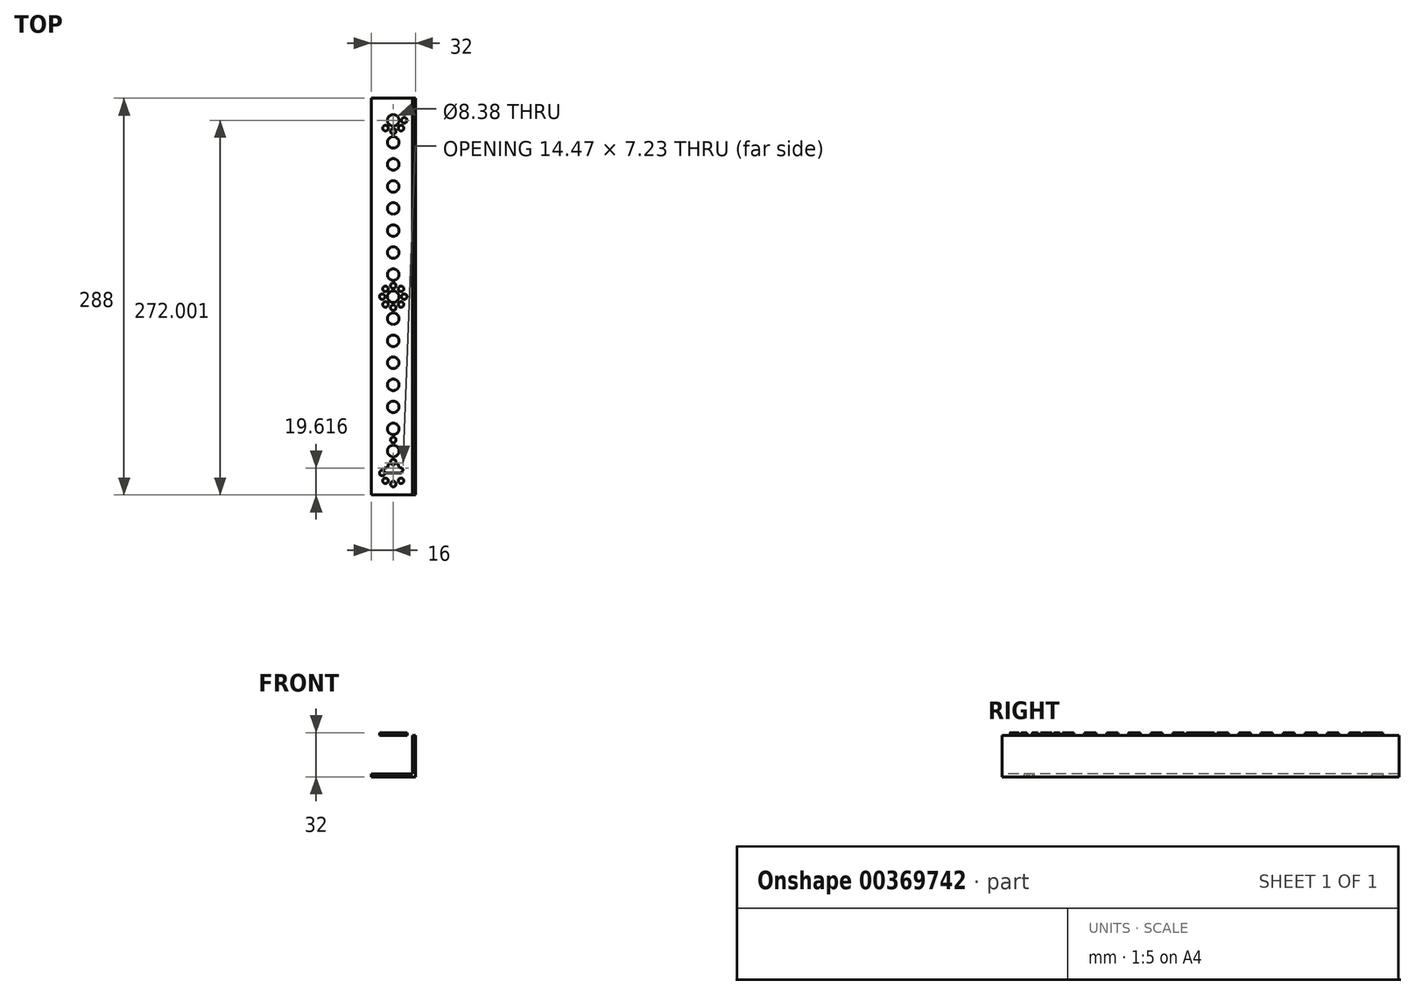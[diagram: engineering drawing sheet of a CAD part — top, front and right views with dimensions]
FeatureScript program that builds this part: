
annotation { "Feature Type Name" : "Feature", "Feature Type Description" : "" }
export const myFeature = defineFeature(function(context is Context, id is Id, definition is map)
    precondition{}
    {
        {
            var Q0;
            Q0=qCreatedBy(makeId("Front.planeOp"),FACE);
            var sketch = newSketch(context, id + "F0", { "sketchPlane" : qUnion([Q0])});
            skLineSegment(sketch, "E0.bottom", {"start": v(0, 0) * mm, "end": v(32, 0) * mm});
            skLineSegment(sketch, "E0.top", {"start": v(0, 32) * mm, "end": v(32, 32) * mm});
            skLineSegment(sketch, "E0.left", {"start": v(0, 0) * mm, "end": v(0, 32) * mm});
            skLineSegment(sketch, "E0.right", {"start": v(32, 0) * mm, "end": v(32, 32) * mm});
            skSolve(sketch);
        }
        {
            var Q0;
            Q0=makeQuery(id+"F0.imprint","IMPRINT",FACE,{"disambiguationData":[TD([[makeQuery(id+"F0.imprint","IMPRINT",EDGE,{"derivedFrom":sQuery(id+"F0.wireOp",EDGE,"E0.bottom")}),1.0]])]});
            extrude(context, id + "F1", {"entities" : qUnion([Q0]), "oppositeDirection" : true, "depth" : 288 * mm});
        }
        {
            var Q0;
            Q0=makeQuery(id+"F1.opExtrude","SWEPT_FACE",FACE,{"disambiguationData":[OSD([sQuery(id+"F0.wireOp",EDGE,"E0.left")])]});
            var Q1;
            Q1=makeQuery(id+"F1.opExtrude","CAP_FACE",FACE,{"disambiguationData":[OSD([sQuery(id+"F0.wireOp",EDGE,"E0.bottom"),sQuery(id+"F0.wireOp",EDGE,"E0.top"),sQuery(id+"F0.wireOp",EDGE,"E0.left"),sQuery(id+"F0.wireOp",EDGE,"E0.right")])],"isStart":true});
            var Q2;
            Q2=makeQuery(id+"F1.opExtrude","CAP_FACE",FACE,{"disambiguationData":[OSD([sQuery(id+"F0.wireOp",EDGE,"E0.bottom"),sQuery(id+"F0.wireOp",EDGE,"E0.top"),sQuery(id+"F0.wireOp",EDGE,"E0.left"),sQuery(id+"F0.wireOp",EDGE,"E0.right")])],"isStart":false});
            shell(context, id + "F2", {"entities" : qUnion([Q0, Q1, Q2]), "thickness" : 2 * mm});
        }
        {
            var Q0;
            Q0=makeQuery(id+"F1.opExtrude","SWEPT_FACE",FACE,{"disambiguationData":[OSD([sQuery(id+"F0.wireOp",EDGE,"E0.bottom")])]});
            var sketch = newSketch(context, id + "F3", { "sketchPlane" : qUnion([Q0])});
            skLineSegment(sketch, "E1.0", {"start": v(0, 0) * mm, "end": v(32, 0) * mm});
            skLineSegment(sketch, "E2.0", {"start": v(0, -288) * mm, "end": v(0, 0) * mm});
            skLineSegment(sketch, "E3.0", {"start": v(32, -288) * mm, "end": v(32, 0) * mm});
            skLineSegment(sketch, "E4.0", {"start": v(0, -288) * mm, "end": v(32, -288) * mm});
            skLineSegment(sketch, "E5", {"start": v(16, 0) * mm, "end": v(16, -288) * mm});
            skLineSegment(sketch, "E6", {"start": v(0, -144) * mm, "end": v(32, -144) * mm});
            skCircle(sketch, "E7", {"center": v(16, -16) * mm, "radius": 4.2 * mm});
            skCircle(sketch, "E8.cCircle", {"center": v(16, -16) * mm, "radius": 8 * mm, "construction": true});
            skLineSegment(sketch, "E8.0", {"start": v(24, -16) * mm, "end": v(21.66, -21.66) * mm});
            skLineSegment(sketch, "E8.1", {"start": v(21.66, -21.66) * mm, "end": v(16, -24) * mm});
            skLineSegment(sketch, "E8.2", {"start": v(16, -24) * mm, "end": v(10.34, -21.66) * mm});
            skLineSegment(sketch, "E8.3", {"start": v(10.34, -21.66) * mm, "end": v(8, -16) * mm});
            skLineSegment(sketch, "E8.4", {"start": v(8, -16) * mm, "end": v(10.34, -10.34) * mm});
            skLineSegment(sketch, "E8.5", {"start": v(10.34, -10.34) * mm, "end": v(16, -8) * mm});
            skLineSegment(sketch, "E8.6", {"start": v(16, -8) * mm, "end": v(21.66, -10.34) * mm});
            skLineSegment(sketch, "E8.7", {"start": v(21.66, -10.34) * mm, "end": v(24, -16) * mm});
            skLineSegment(sketch, "E9", {"start": v(16, -16) * mm, "end": v(32, -16) * mm});
            skLineSegment(sketch, "E10", {"start": v(32, -16) * mm, "end": v(0, -16) * mm});
            skCircle(sketch, "E11", {"center": v(16, -8) * mm, "radius": 2 * mm});
            skCircle(sketch, "E12", {"center": v(21.66, -10.34) * mm, "radius": 2 * mm});
            skCircle(sketch, "E13", {"center": v(24, -16) * mm, "radius": 2 * mm});
            skCircle(sketch, "E14", {"center": v(10.34, -10.34) * mm, "radius": 2 * mm});
            skCircle(sketch, "E15", {"center": v(8, -16) * mm, "radius": 2 * mm});
            skCircle(sketch, "E16.MirrorC", {"center": v(10.34, -21.66) * mm, "radius": 2 * mm});
            skCircle(sketch, "E17.MirrorC", {"center": v(16, -24) * mm, "radius": 2 * mm});
            skCircle(sketch, "E18.MirrorC", {"center": v(21.66, -21.66) * mm, "radius": 2 * mm});
            skCircle(sketch, "E19.MirrorC", {"center": v(10.34, -277.66) * mm, "radius": 2 * mm});
            skCircle(sketch, "E20.MirrorC", {"center": v(16, -280) * mm, "radius": 2 * mm});
            skCircle(sketch, "E21.MirrorC", {"center": v(21.66, -277.66) * mm, "radius": 2 * mm});
            skCircle(sketch, "E22.MirrorC", {"center": v(24, -272) * mm, "radius": 2 * mm});
            skCircle(sketch, "E23.MirrorC", {"center": v(21.66, -266.34) * mm, "radius": 2 * mm});
            skCircle(sketch, "E24.MirrorC", {"center": v(16, -264) * mm, "radius": 2 * mm});
            skCircle(sketch, "E25.MirrorC", {"center": v(10.34, -266.34) * mm, "radius": 2 * mm});
            skCircle(sketch, "E26.MirrorC", {"center": v(16, -272) * mm, "radius": 4.2 * mm});
            skCircle(sketch, "E27.MirrorC", {"center": v(8, -272) * mm, "radius": 2 * mm});
            skSolve(sketch);
        }
        {
            var Q0;
            {var subQ0=sQuery(id+"F3.wireOp",EDGE,"E10");var subQ1=sQuery(id+"F3.wireOp",EDGE,"E5");var subQ2=makeQuery(id+"F3.imprint","INTERSECT",VERTEX,{"derivedFrom":[subQ1,subQ0]});Q0=makeQuery(id+"F3.imprint","IMPRINT",FACE,{"disambiguationData":[TD([[makeQuery(id+"F3.imprint","IMPRINT",EDGE,{"disambiguationData":[TD([[subQ2,-1.0]])],"derivedFrom":subQ1}),1.0]])]});}
            var Q1;
            {var subQ0=sQuery(id+"F3.wireOp",EDGE,"E7");var subQ1=sQuery(id+"F3.wireOp",EDGE,"E5");var subQ2=makeQuery(id+"F3.imprint","INTERSECT",VERTEX,{"disambiguationData":[OD(0.0)],"derivedFrom":[subQ1,subQ0]});Q1=makeQuery(id+"F3.imprint","IMPRINT",FACE,{"disambiguationData":[TD([[makeQuery(id+"F3.imprint","IMPRINT",EDGE,{"disambiguationData":[TD([[subQ2,-1.0]])],"derivedFrom":subQ1}),1.0]])]});}
            var Q2;
            {var subQ0=sQuery(id+"F3.wireOp",EDGE,"E7");var subQ1=sQuery(id+"F3.wireOp",EDGE,"E5");var subQ2=makeQuery(id+"F3.imprint","INTERSECT",VERTEX,{"disambiguationData":[OD(0.0)],"derivedFrom":[subQ1,subQ0]});Q2=makeQuery(id+"F3.imprint","IMPRINT",FACE,{"disambiguationData":[TD([[makeQuery(id+"F3.imprint","IMPRINT",EDGE,{"disambiguationData":[TD([[subQ2,-1.0]])],"derivedFrom":subQ1}),-1.0]])]});}
            var Q3;
            {var subQ0=sQuery(id+"F3.wireOp",EDGE,"E10");var subQ1=sQuery(id+"F3.wireOp",EDGE,"E5");var subQ2=makeQuery(id+"F3.imprint","INTERSECT",VERTEX,{"derivedFrom":[subQ1,subQ0]});Q3=makeQuery(id+"F3.imprint","IMPRINT",FACE,{"disambiguationData":[TD([[makeQuery(id+"F3.imprint","IMPRINT",EDGE,{"disambiguationData":[TD([[subQ2,-1.0]])],"derivedFrom":subQ1}),-1.0]])]});}
            var Q4;
            {var subQ0=sQuery(id+"F3.wireOp",EDGE,"E26.MirrorC");var subQ1=sQuery(id+"F3.wireOp",EDGE,"E5");var subQ2=makeQuery(id+"F3.imprint","INTERSECT",VERTEX,{"disambiguationData":[OD(0.0)],"derivedFrom":[subQ1,subQ0]});Q4=makeQuery(id+"F3.imprint","IMPRINT",FACE,{"disambiguationData":[TD([[makeQuery(id+"F3.imprint","IMPRINT",EDGE,{"disambiguationData":[TD([[subQ2,-1.0]])],"derivedFrom":subQ1}),1.0]])]});}
            var Q5;
            {var subQ0=sQuery(id+"F3.wireOp",EDGE,"E26.MirrorC");var subQ1=sQuery(id+"F3.wireOp",EDGE,"E5");var subQ2=makeQuery(id+"F3.imprint","INTERSECT",VERTEX,{"disambiguationData":[OD(0.0)],"derivedFrom":[subQ1,subQ0]});Q5=makeQuery(id+"F3.imprint","IMPRINT",FACE,{"disambiguationData":[TD([[makeQuery(id+"F3.imprint","IMPRINT",EDGE,{"disambiguationData":[TD([[subQ2,-1.0]])],"derivedFrom":subQ1}),-1.0]])]});}
            var Q6;
            Q6=makeQuery(id+"F2.opShell","OFFSET_FACE",FACE,{"disambiguationData":[OSD([sQuery(id+"F0.wireOp",EDGE,"E0.bottom")])]});
            extrude(context, id + "F4", {"entities" : qUnion([Q0, Q1, Q2, Q3, Q4, Q5]), "operationType" : NewBodyOperationType.REMOVE, "endBound" : BoundingType.UP_TO_SURFACE, "oppositeDirection" : true, "endBoundEntityFace" : qUnion([Q6]), "depth" : 25.4 * mm});
        }
        {
            var Q0;
            Q0=makeQuery(id+"F1.opExtrude","SWEPT_FACE",FACE,{"disambiguationData":[OSD([sQuery(id+"F0.wireOp",EDGE,"E0.top")])]});
            var sketch = newSketch(context, id + "F5", { "sketchPlane" : qUnion([Q0])});
            skLineSegment(sketch, "E28.0", {"start": v(16, 0) * mm, "end": v(16, 288) * mm});
            skLineSegment(sketch, "E29.0", {"start": v(32, 16) * mm, "end": v(0, 16) * mm});
            skCircle(sketch, "E30.0", {"center": v(10.34, 21.66) * mm, "radius": 2 * mm});
            skCircle(sketch, "E31.0", {"center": v(8, 16) * mm, "radius": 2 * mm});
            skCircle(sketch, "E32.0", {"center": v(10.34, 10.34) * mm, "radius": 2 * mm});
            skCircle(sketch, "E33.0", {"center": v(16, 8) * mm, "radius": 2 * mm});
            skCircle(sketch, "E34.0", {"center": v(21.66, 10.34) * mm, "radius": 2 * mm});
            skCircle(sketch, "E35.0", {"center": v(24, 16) * mm, "radius": 2 * mm});
            skCircle(sketch, "E36.0", {"center": v(21.66, 21.66) * mm, "radius": 2 * mm});
            skLineSegment(sketch, "E37.0", {"start": v(32, 288) * mm, "end": v(32, 0) * mm});
            skCircle(sketch, "E38.0", {"center": v(10.34, 277.66) * mm, "radius": 2 * mm});
            skCircle(sketch, "E39.0", {"center": v(8, 272) * mm, "radius": 2 * mm});
            skCircle(sketch, "E40.0", {"center": v(10.34, 266.34) * mm, "radius": 2 * mm});
            skCircle(sketch, "E41.0", {"center": v(16, 272) * mm, "radius": 4.2 * mm});
            skCircle(sketch, "E42.0", {"center": v(16, 264) * mm, "radius": 2 * mm});
            skCircle(sketch, "E43.0", {"center": v(21.66, 266.34) * mm, "radius": 2 * mm});
            skArc(sketch, "E44.0.0", {"start": v(16, 267.81) * mm, "mid": v(20.2, 272) * mm, "end": v(16, 276.2) * mm});
            skLineSegment(sketch, "E44.0.1", {"start": v(16, 276.2) * mm, "end": v(16, 278) * mm});
            skArc(sketch, "E44.0.2", {"start": v(16, 278) * mm, "mid": v(18, 280) * mm, "end": v(16, 282) * mm});
            skLineSegment(sketch, "E44.0.3", {"start": v(16, 282) * mm, "end": v(16, 288) * mm});
            skLineSegment(sketch, "E44.0.4", {"start": v(16, 288) * mm, "end": v(32, 288) * mm});
            skLineSegment(sketch, "E44.0.5", {"start": v(32, 288) * mm, "end": v(32, 144) * mm});
            skLineSegment(sketch, "E44.0.6", {"start": v(32, 144) * mm, "end": v(16, 144) * mm});
            skLineSegment(sketch, "E44.0.7", {"start": v(16, 144) * mm, "end": v(16, 262) * mm});
            skArc(sketch, "E44.0.8", {"start": v(16, 262) * mm, "mid": v(18, 264) * mm, "end": v(16, 266) * mm});
            skLineSegment(sketch, "E44.0.9", {"start": v(16, 266) * mm, "end": v(16, 267.81) * mm});
            skCircle(sketch, "E45.0", {"center": v(24, 272) * mm, "radius": 2 * mm});
            skCircle(sketch, "E46.0", {"center": v(21.66, 277.66) * mm, "radius": 2 * mm});
            skLineSegment(sketch, "E47.0.0", {"start": v(16, 278) * mm, "end": v(16, 276.2) * mm});
            skArc(sketch, "E47.0.1", {"start": v(16, 276.2) * mm, "mid": v(11.8, 272) * mm, "end": v(16, 267.81) * mm});
            skLineSegment(sketch, "E47.0.2", {"start": v(16, 267.81) * mm, "end": v(16, 266) * mm});
            skArc(sketch, "E47.0.3", {"start": v(16, 266) * mm, "mid": v(14, 264) * mm, "end": v(16, 262) * mm});
            skLineSegment(sketch, "E47.0.4", {"start": v(16, 262) * mm, "end": v(16, 144) * mm});
            skLineSegment(sketch, "E47.0.5", {"start": v(16, 144) * mm, "end": v(0, 144) * mm});
            skLineSegment(sketch, "E47.0.6", {"start": v(0, 144) * mm, "end": v(0, 288) * mm});
            skLineSegment(sketch, "E47.0.7", {"start": v(0, 288) * mm, "end": v(16, 288) * mm});
            skLineSegment(sketch, "E47.0.8", {"start": v(16, 288) * mm, "end": v(16, 282) * mm});
            skArc(sketch, "E47.0.9", {"start": v(16, 282) * mm, "mid": v(14, 280) * mm, "end": v(16, 278) * mm});
            skCircle(sketch, "E48.0", {"center": v(16, 24) * mm, "radius": 2 * mm});
            skCircle(sketch, "E49.0", {"center": v(16, 16) * mm, "radius": 4.2 * mm});
            skLineSegment(sketch, "E50", {"start": v(0, 216) * mm, "end": v(32, 216) * mm});
            skLineSegment(sketch, "E51.0", {"start": v(0, 288) * mm, "end": v(0, 0) * mm});
            skCircle(sketch, "E52.0", {"center": v(10.34, 149.66) * mm, "radius": 2 * mm});
            skCircle(sketch, "E53.0", {"center": v(8, 144) * mm, "radius": 2 * mm});
            skCircle(sketch, "E54.0", {"center": v(10.34, 138.34) * mm, "radius": 2 * mm});
            skCircle(sketch, "E55.0", {"center": v(16, 136) * mm, "radius": 2 * mm});
            skCircle(sketch, "E56.0", {"center": v(21.66, 138.34) * mm, "radius": 2 * mm});
            skCircle(sketch, "E57.0", {"center": v(24, 144) * mm, "radius": 2 * mm});
            skCircle(sketch, "E58.0", {"center": v(21.66, 149.66) * mm, "radius": 2 * mm});
            skCircle(sketch, "E59.0", {"center": v(16, 152) * mm, "radius": 2 * mm});
            skCircle(sketch, "E60.0", {"center": v(16, 144) * mm, "radius": 4.2 * mm});
            skLineSegment(sketch, "E61", {"start": v(16, 24) * mm, "end": v(16, 32) * mm});
            skCircle(sketch, "E62.0", {"center": v(34.9, 49.18) * mm, "radius": 2 * mm});
            skCircle(sketch, "E63.0", {"center": v(16, 40) * mm, "radius": 2 * mm});
            skCircle(sketch, "E64.0", {"center": v(34.9, 37.87) * mm, "radius": 2 * mm});
            skCircle(sketch, "E65.0", {"center": v(40.55, 35.52) * mm, "radius": 2 * mm});
            skCircle(sketch, "E66.0", {"center": v(46.21, 37.87) * mm, "radius": 2 * mm});
            skCircle(sketch, "E67.0", {"center": v(48.55, 43.52) * mm, "radius": 2 * mm});
            skCircle(sketch, "E68.0", {"center": v(46.21, 49.18) * mm, "radius": 2 * mm});
            skCircle(sketch, "E69.0", {"center": v(40.55, 51.52) * mm, "radius": 2 * mm});
            skCircle(sketch, "E70.0", {"center": v(16, 32) * mm, "radius": 4.2 * mm});
            skLineSegment(sketch, "E71", {"start": v(16, 32) * mm, "end": v(16, 40) * mm});
            skLineSegment(sketch, "E72", {"start": v(16, 40) * mm, "end": v(16, 48) * mm});
            skCircle(sketch, "E73.0", {"center": v(16, 48) * mm, "radius": 4.2 * mm});
            skLineSegment(sketch, "E74", {"start": v(16, 48) * mm, "end": v(16, 64) * mm});
            skCircle(sketch, "E75.0", {"center": v(16, 64) * mm, "radius": 4.2 * mm});
            skLineSegment(sketch, "E76", {"start": v(16, 64) * mm, "end": v(16, 80) * mm});
            skCircle(sketch, "E77.0", {"center": v(16, 80) * mm, "radius": 4.2 * mm});
            skLineSegment(sketch, "E78", {"start": v(16, 80) * mm, "end": v(16, 96) * mm});
            skCircle(sketch, "E79.0", {"center": v(16, 96) * mm, "radius": 4.2 * mm});
            skLineSegment(sketch, "E80", {"start": v(16, 96) * mm, "end": v(16, 112) * mm});
            skCircle(sketch, "E81.0", {"center": v(16, 112) * mm, "radius": 4.2 * mm});
            skLineSegment(sketch, "E82", {"start": v(16, 112) * mm, "end": v(16, 128) * mm});
            skCircle(sketch, "E83.0", {"center": v(16, 128) * mm, "radius": 4.2 * mm});
            skCircle(sketch, "E84.MirrorC", {"center": v(16, 160) * mm, "radius": 4.2 * mm});
            skCircle(sketch, "E85.MirrorC", {"center": v(16, 176) * mm, "radius": 4.2 * mm});
            skCircle(sketch, "E86.MirrorC", {"center": v(16, 192) * mm, "radius": 4.2 * mm});
            skCircle(sketch, "E87.MirrorC", {"center": v(16, 208) * mm, "radius": 4.2 * mm});
            skCircle(sketch, "E88.MirrorC", {"center": v(16, 224) * mm, "radius": 4.2 * mm});
            skCircle(sketch, "E89.MirrorC", {"center": v(16, 240) * mm, "radius": 4.2 * mm});
            skCircle(sketch, "E90.MirrorC", {"center": v(16, 256) * mm, "radius": 4.2 * mm});
            skSolve(sketch);
        }
        {
            var Q0;
            {var subQ0=sQuery(id+"F5.wireOp",EDGE,"E74");var subQ1=sQuery(id+"F5.wireOp",EDGE,"E72");var subQ2=makeQuery(id+"F5.imprint","INTERSECT",VERTEX,{"derivedFrom":[subQ1,subQ0]});Q0=makeQuery(id+"F5.imprint","IMPRINT",FACE,{"disambiguationData":[TD([[makeQuery(id+"F5.imprint","IMPRINT",EDGE,{"disambiguationData":[TD([[subQ2,1.0]])],"derivedFrom":subQ1}),-1.0]])]});}
            var Q1;
            {var subQ0=sQuery(id+"F5.wireOp",EDGE,"E74");var subQ1=sQuery(id+"F5.wireOp",EDGE,"E72");var subQ2=makeQuery(id+"F5.imprint","INTERSECT",VERTEX,{"derivedFrom":[subQ1,subQ0]});Q1=makeQuery(id+"F5.imprint","IMPRINT",FACE,{"disambiguationData":[TD([[makeQuery(id+"F5.imprint","IMPRINT",EDGE,{"disambiguationData":[TD([[subQ2,1.0]])],"derivedFrom":subQ1}),1.0]])]});}
            var Q2;
            {var subQ0=sQuery(id+"F5.wireOp",EDGE,"E71");var subQ1=sQuery(id+"F5.wireOp",EDGE,"E61");var subQ2=makeQuery(id+"F5.imprint","INTERSECT",VERTEX,{"derivedFrom":[subQ1,subQ0]});Q2=makeQuery(id+"F5.imprint","IMPRINT",FACE,{"disambiguationData":[TD([[makeQuery(id+"F5.imprint","IMPRINT",EDGE,{"disambiguationData":[TD([[subQ2,1.0]])],"derivedFrom":subQ1}),-1.0]])]});}
            var Q3;
            {var subQ0=sQuery(id+"F5.wireOp",EDGE,"E71");var subQ1=sQuery(id+"F5.wireOp",EDGE,"E61");var subQ2=makeQuery(id+"F5.imprint","INTERSECT",VERTEX,{"derivedFrom":[subQ1,subQ0]});Q3=makeQuery(id+"F5.imprint","IMPRINT",FACE,{"disambiguationData":[TD([[makeQuery(id+"F5.imprint","IMPRINT",EDGE,{"disambiguationData":[TD([[subQ2,1.0]])],"derivedFrom":subQ1}),1.0]])]});}
            var Q4;
            {var subQ0=sQuery(id+"F5.wireOp",EDGE,"E61");var subQ1=sQuery(id+"F5.wireOp",EDGE,"E28.0");var subQ2=makeQuery(id+"F5.imprint","INTERSECT",VERTEX,{"derivedFrom":[subQ1,subQ0]});Q4=makeQuery(id+"F5.imprint","IMPRINT",FACE,{"disambiguationData":[TD([[makeQuery(id+"F5.imprint","IMPRINT",EDGE,{"disambiguationData":[TD([[subQ2,1.0]])],"derivedFrom":subQ1}),-1.0]])]});}
            var Q5;
            {var subQ0=sQuery(id+"F5.wireOp",EDGE,"E61");var subQ1=sQuery(id+"F5.wireOp",EDGE,"E28.0");var subQ2=makeQuery(id+"F5.imprint","INTERSECT",VERTEX,{"derivedFrom":[subQ1,subQ0]});Q5=makeQuery(id+"F5.imprint","IMPRINT",FACE,{"disambiguationData":[TD([[makeQuery(id+"F5.imprint","IMPRINT",EDGE,{"disambiguationData":[TD([[subQ2,1.0]])],"derivedFrom":subQ1}),1.0]])]});}
            var Q6;
            {var subQ0=sQuery(id+"F5.wireOp",EDGE,"E49.0");var subQ1=sQuery(id+"F5.wireOp",EDGE,"E29.0");var subQ2=makeQuery(id+"F5.imprint","INTERSECT",VERTEX,{"disambiguationData":[OD(0.0)],"derivedFrom":[subQ1,subQ0]});Q6=makeQuery(id+"F5.imprint","IMPRINT",FACE,{"disambiguationData":[TD([[makeQuery(id+"F5.imprint","IMPRINT",EDGE,{"disambiguationData":[TD([[subQ2,-1.0]])],"derivedFrom":subQ1}),-1.0]])]});}
            var Q7;
            {var subQ0=sQuery(id+"F5.wireOp",EDGE,"E35.0");var subQ1=sQuery(id+"F5.wireOp",EDGE,"E29.0");var subQ2=makeQuery(id+"F5.imprint","INTERSECT",VERTEX,{"disambiguationData":[OD(0.0)],"derivedFrom":[subQ1,subQ0]});Q7=makeQuery(id+"F5.imprint","IMPRINT",FACE,{"disambiguationData":[TD([[makeQuery(id+"F5.imprint","IMPRINT",EDGE,{"disambiguationData":[TD([[subQ2,-1.0]])],"derivedFrom":subQ1}),1.0]])]});}
            var Q8;
            {var subQ0=sQuery(id+"F5.wireOp",EDGE,"E35.0");var subQ1=sQuery(id+"F5.wireOp",EDGE,"E29.0");var subQ2=makeQuery(id+"F5.imprint","INTERSECT",VERTEX,{"disambiguationData":[OD(0.0)],"derivedFrom":[subQ1,subQ0]});Q8=makeQuery(id+"F5.imprint","IMPRINT",FACE,{"disambiguationData":[TD([[makeQuery(id+"F5.imprint","IMPRINT",EDGE,{"disambiguationData":[TD([[subQ2,-1.0]])],"derivedFrom":subQ1}),-1.0]])]});}
            var Q9;
            Q9=makeQuery(id+"F5.imprint","IMPRINT",FACE,{"disambiguationData":[TD([[makeQuery(id+"F5.imprint","IMPRINT",EDGE,{"derivedFrom":sQuery(id+"F5.wireOp",EDGE,"E36.0")}),1.0]])]});
            var Q10;
            {var subQ0=sQuery(id+"F5.wireOp",EDGE,"E49.0");var subQ1=sQuery(id+"F5.wireOp",EDGE,"E29.0");var subQ2=makeQuery(id+"F5.imprint","INTERSECT",VERTEX,{"disambiguationData":[OD(0.0)],"derivedFrom":[subQ1,subQ0]});Q10=makeQuery(id+"F5.imprint","IMPRINT",FACE,{"disambiguationData":[TD([[makeQuery(id+"F5.imprint","IMPRINT",EDGE,{"disambiguationData":[TD([[subQ2,-1.0]])],"derivedFrom":subQ1}),1.0]])]});}
            var Q11;
            Q11=makeQuery(id+"F5.imprint","IMPRINT",FACE,{"disambiguationData":[TD([[makeQuery(id+"F5.imprint","IMPRINT",EDGE,{"derivedFrom":sQuery(id+"F5.wireOp",EDGE,"E30.0")}),1.0]])]});
            var Q12;
            {var subQ0=sQuery(id+"F5.wireOp",EDGE,"E31.0");var subQ1=sQuery(id+"F5.wireOp",EDGE,"E29.0");var subQ2=makeQuery(id+"F5.imprint","INTERSECT",VERTEX,{"disambiguationData":[OD(0.0)],"derivedFrom":[subQ1,subQ0]});Q12=makeQuery(id+"F5.imprint","IMPRINT",FACE,{"disambiguationData":[TD([[makeQuery(id+"F5.imprint","IMPRINT",EDGE,{"disambiguationData":[TD([[subQ2,-1.0]])],"derivedFrom":subQ1}),1.0]])]});}
            var Q13;
            {var subQ0=sQuery(id+"F5.wireOp",EDGE,"E31.0");var subQ1=sQuery(id+"F5.wireOp",EDGE,"E29.0");var subQ2=makeQuery(id+"F5.imprint","INTERSECT",VERTEX,{"disambiguationData":[OD(0.0)],"derivedFrom":[subQ1,subQ0]});Q13=makeQuery(id+"F5.imprint","IMPRINT",FACE,{"disambiguationData":[TD([[makeQuery(id+"F5.imprint","IMPRINT",EDGE,{"disambiguationData":[TD([[subQ2,-1.0]])],"derivedFrom":subQ1}),-1.0]])]});}
            var Q14;
            Q14=makeQuery(id+"F5.imprint","IMPRINT",FACE,{"disambiguationData":[TD([[makeQuery(id+"F5.imprint","IMPRINT",EDGE,{"derivedFrom":sQuery(id+"F5.wireOp",EDGE,"E32.0")}),-1.0]])]});
            var Q15;
            {var subQ0=sQuery(id+"F5.wireOp",EDGE,"E28.0");var subQ1=sQuery(id+"F5.wireOp",EDGE,"E33.0");var subQ2=makeQuery(id+"F5.imprint","INTERSECT",VERTEX,{"disambiguationData":[OD(0.0)],"derivedFrom":[subQ1,subQ0]});Q15=makeQuery(id+"F5.imprint","IMPRINT",FACE,{"disambiguationData":[TD([[makeQuery(id+"F5.imprint","IMPRINT",EDGE,{"disambiguationData":[TD([[subQ2,1.0]])],"derivedFrom":subQ1}),-1.0]])]});}
            var Q16;
            {var subQ0=sQuery(id+"F5.wireOp",EDGE,"E28.0");var subQ1=sQuery(id+"F5.wireOp",EDGE,"E33.0");var subQ2=makeQuery(id+"F5.imprint","INTERSECT",VERTEX,{"disambiguationData":[OD(0.0)],"derivedFrom":[subQ1,subQ0]});Q16=makeQuery(id+"F5.imprint","IMPRINT",FACE,{"disambiguationData":[TD([[makeQuery(id+"F5.imprint","IMPRINT",EDGE,{"disambiguationData":[TD([[subQ2,-1.0]])],"derivedFrom":subQ1}),-1.0]])]});}
            var Q17;
            Q17=makeQuery(id+"F5.imprint","IMPRINT",FACE,{"disambiguationData":[TD([[makeQuery(id+"F5.imprint","IMPRINT",EDGE,{"derivedFrom":sQuery(id+"F5.wireOp",EDGE,"E34.0")}),-1.0]])]});
            var Q18;
            {var subQ0=sQuery(id+"F5.wireOp",EDGE,"E78");var subQ1=sQuery(id+"F5.wireOp",EDGE,"E76");var subQ2=makeQuery(id+"F5.imprint","INTERSECT",VERTEX,{"derivedFrom":[subQ1,subQ0]});Q18=makeQuery(id+"F5.imprint","IMPRINT",FACE,{"disambiguationData":[TD([[makeQuery(id+"F5.imprint","IMPRINT",EDGE,{"disambiguationData":[TD([[subQ2,1.0]])],"derivedFrom":subQ1}),1.0]])]});}
            var Q19;
            {var subQ0=sQuery(id+"F5.wireOp",EDGE,"E76");var subQ1=sQuery(id+"F5.wireOp",EDGE,"E74");var subQ2=makeQuery(id+"F5.imprint","INTERSECT",VERTEX,{"derivedFrom":[subQ1,subQ0]});Q19=makeQuery(id+"F5.imprint","IMPRINT",FACE,{"disambiguationData":[TD([[makeQuery(id+"F5.imprint","IMPRINT",EDGE,{"disambiguationData":[TD([[subQ2,1.0]])],"derivedFrom":subQ1}),1.0]])]});}
            var Q20;
            {var subQ0=sQuery(id+"F5.wireOp",EDGE,"E78");var subQ1=sQuery(id+"F5.wireOp",EDGE,"E76");var subQ2=makeQuery(id+"F5.imprint","INTERSECT",VERTEX,{"derivedFrom":[subQ1,subQ0]});Q20=makeQuery(id+"F5.imprint","IMPRINT",FACE,{"disambiguationData":[TD([[makeQuery(id+"F5.imprint","IMPRINT",EDGE,{"disambiguationData":[TD([[subQ2,1.0]])],"derivedFrom":subQ1}),-1.0]])]});}
            var Q21;
            {var subQ0=sQuery(id+"F5.wireOp",EDGE,"E76");var subQ1=sQuery(id+"F5.wireOp",EDGE,"E74");var subQ2=makeQuery(id+"F5.imprint","INTERSECT",VERTEX,{"derivedFrom":[subQ1,subQ0]});Q21=makeQuery(id+"F5.imprint","IMPRINT",FACE,{"disambiguationData":[TD([[makeQuery(id+"F5.imprint","IMPRINT",EDGE,{"disambiguationData":[TD([[subQ2,1.0]])],"derivedFrom":subQ1}),-1.0]])]});}
            var Q22;
            {var subQ0=sQuery(id+"F5.wireOp",EDGE,"E80");var subQ1=sQuery(id+"F5.wireOp",EDGE,"E78");var subQ2=makeQuery(id+"F5.imprint","INTERSECT",VERTEX,{"derivedFrom":[subQ1,subQ0]});Q22=makeQuery(id+"F5.imprint","IMPRINT",FACE,{"disambiguationData":[TD([[makeQuery(id+"F5.imprint","IMPRINT",EDGE,{"disambiguationData":[TD([[subQ2,1.0]])],"derivedFrom":subQ1}),-1.0]])]});}
            var Q23;
            {var subQ0=sQuery(id+"F5.wireOp",EDGE,"E80");var subQ1=sQuery(id+"F5.wireOp",EDGE,"E78");var subQ2=makeQuery(id+"F5.imprint","INTERSECT",VERTEX,{"derivedFrom":[subQ1,subQ0]});Q23=makeQuery(id+"F5.imprint","IMPRINT",FACE,{"disambiguationData":[TD([[makeQuery(id+"F5.imprint","IMPRINT",EDGE,{"disambiguationData":[TD([[subQ2,1.0]])],"derivedFrom":subQ1}),1.0]])]});}
            var Q24;
            {var subQ0=sQuery(id+"F5.wireOp",EDGE,"E82");var subQ1=sQuery(id+"F5.wireOp",EDGE,"E80");var subQ2=makeQuery(id+"F5.imprint","INTERSECT",VERTEX,{"derivedFrom":[subQ1,subQ0]});Q24=makeQuery(id+"F5.imprint","IMPRINT",FACE,{"disambiguationData":[TD([[makeQuery(id+"F5.imprint","IMPRINT",EDGE,{"disambiguationData":[TD([[subQ2,1.0]])],"derivedFrom":subQ1}),1.0]])]});}
            var Q25;
            {var subQ0=sQuery(id+"F5.wireOp",EDGE,"E82");var subQ1=sQuery(id+"F5.wireOp",EDGE,"E80");var subQ2=makeQuery(id+"F5.imprint","INTERSECT",VERTEX,{"derivedFrom":[subQ1,subQ0]});Q25=makeQuery(id+"F5.imprint","IMPRINT",FACE,{"disambiguationData":[TD([[makeQuery(id+"F5.imprint","IMPRINT",EDGE,{"disambiguationData":[TD([[subQ2,1.0]])],"derivedFrom":subQ1}),-1.0]])]});}
            var Q26;
            {var subQ0=sQuery(id+"F5.wireOp",EDGE,"E82");var subQ1=sQuery(id+"F5.wireOp",EDGE,"E28.0");var subQ2=makeQuery(id+"F5.imprint","INTERSECT",VERTEX,{"derivedFrom":[subQ1,subQ0]});Q26=makeQuery(id+"F5.imprint","IMPRINT",FACE,{"disambiguationData":[TD([[makeQuery(id+"F5.imprint","IMPRINT",EDGE,{"disambiguationData":[TD([[subQ2,-1.0]])],"derivedFrom":subQ1}),-1.0]])]});}
            var Q27;
            {var subQ0=sQuery(id+"F5.wireOp",EDGE,"E82");var subQ1=sQuery(id+"F5.wireOp",EDGE,"E28.0");var subQ2=makeQuery(id+"F5.imprint","INTERSECT",VERTEX,{"derivedFrom":[subQ1,subQ0]});Q27=makeQuery(id+"F5.imprint","IMPRINT",FACE,{"disambiguationData":[TD([[makeQuery(id+"F5.imprint","IMPRINT",EDGE,{"disambiguationData":[TD([[subQ2,-1.0]])],"derivedFrom":subQ1}),1.0]])]});}
            var Q28;
            {var subQ1=sQuery(id+"F5.wireOp",EDGE,"E47.0.4");var subQ3=sQuery(id+"F5.wireOp",EDGE,"E60.0");var subQ4=makeQuery(id+"F5.imprint","INTERSECT",VERTEX,{"derivedFrom":[subQ1,subQ3]});Q28=makeQuery(id+"F5.imprint","IMPRINT",FACE,{"disambiguationData":[TD([[makeQuery(id+"F5.imprint","IMPRINT",EDGE,{"disambiguationData":[TD([[subQ4,1.0]])],"derivedFrom":subQ3}),-1.0]])]});}
            var Q29;
            {var subQ1=sQuery(id+"F5.wireOp",EDGE,"E44.0.6");var subQ3=sQuery(id+"F5.wireOp",EDGE,"E60.0");var subQ4=makeQuery(id+"F5.imprint","INTERSECT",VERTEX,{"derivedFrom":[subQ1,subQ3]});Q29=makeQuery(id+"F5.imprint","IMPRINT",FACE,{"disambiguationData":[TD([[makeQuery(id+"F5.imprint","IMPRINT",EDGE,{"disambiguationData":[TD([[subQ4,1.0]])],"derivedFrom":subQ3}),-1.0]])]});}
            var Q30;
            {var subQ1=sQuery(id+"F5.wireOp",EDGE,"E28.0");var subQ3=sQuery(id+"F5.wireOp",EDGE,"E60.0");var subQ4=makeQuery(id+"F5.imprint","INTERSECT",VERTEX,{"derivedFrom":[subQ1,subQ3]});Q30=makeQuery(id+"F5.imprint","IMPRINT",FACE,{"disambiguationData":[TD([[makeQuery(id+"F5.imprint","IMPRINT",EDGE,{"disambiguationData":[TD([[subQ4,1.0]])],"derivedFrom":subQ3}),-1.0]])]});}
            var Q31;
            {var subQ1=sQuery(id+"F5.wireOp",EDGE,"E28.0");var subQ3=sQuery(id+"F5.wireOp",EDGE,"E60.0");var subQ4=makeQuery(id+"F5.imprint","INTERSECT",VERTEX,{"derivedFrom":[subQ1,subQ3]});Q31=makeQuery(id+"F5.imprint","IMPRINT",FACE,{"disambiguationData":[TD([[makeQuery(id+"F5.imprint","IMPRINT",EDGE,{"disambiguationData":[TD([[subQ4,-1.0]])],"derivedFrom":subQ3}),-1.0]])]});}
            var Q32;
            {var subQ0=sQuery(id+"F5.wireOp",EDGE,"E84.MirrorC");var subQ1=sQuery(id+"F5.wireOp",EDGE,"E47.0.4");var subQ2=makeQuery(id+"F5.imprint","INTERSECT",VERTEX,{"disambiguationData":[OD(0.0)],"derivedFrom":[subQ1,subQ0]});Q32=makeQuery(id+"F5.imprint","IMPRINT",FACE,{"disambiguationData":[TD([[makeQuery(id+"F5.imprint","IMPRINT",EDGE,{"disambiguationData":[TD([[subQ2,-1.0]])],"derivedFrom":subQ1}),-1.0]])]});}
            var Q33;
            {var subQ0=sQuery(id+"F5.wireOp",EDGE,"E84.MirrorC");var subQ1=sQuery(id+"F5.wireOp",EDGE,"E47.0.4");var subQ2=makeQuery(id+"F5.imprint","INTERSECT",VERTEX,{"disambiguationData":[OD(0.0)],"derivedFrom":[subQ1,subQ0]});Q33=makeQuery(id+"F5.imprint","IMPRINT",FACE,{"disambiguationData":[TD([[makeQuery(id+"F5.imprint","IMPRINT",EDGE,{"disambiguationData":[TD([[subQ2,-1.0]])],"derivedFrom":subQ1}),1.0]])]});}
            var Q34;
            {var subQ0=sQuery(id+"F5.wireOp",EDGE,"E85.MirrorC");var subQ1=sQuery(id+"F5.wireOp",EDGE,"E47.0.4");var subQ2=makeQuery(id+"F5.imprint","INTERSECT",VERTEX,{"disambiguationData":[OD(0.0)],"derivedFrom":[subQ1,subQ0]});Q34=makeQuery(id+"F5.imprint","IMPRINT",FACE,{"disambiguationData":[TD([[makeQuery(id+"F5.imprint","IMPRINT",EDGE,{"disambiguationData":[TD([[subQ2,-1.0]])],"derivedFrom":subQ1}),-1.0]])]});}
            var Q35;
            {var subQ0=sQuery(id+"F5.wireOp",EDGE,"E85.MirrorC");var subQ1=sQuery(id+"F5.wireOp",EDGE,"E47.0.4");var subQ2=makeQuery(id+"F5.imprint","INTERSECT",VERTEX,{"disambiguationData":[OD(0.0)],"derivedFrom":[subQ1,subQ0]});Q35=makeQuery(id+"F5.imprint","IMPRINT",FACE,{"disambiguationData":[TD([[makeQuery(id+"F5.imprint","IMPRINT",EDGE,{"disambiguationData":[TD([[subQ2,-1.0]])],"derivedFrom":subQ1}),1.0]])]});}
            var Q36;
            {var subQ0=sQuery(id+"F5.wireOp",EDGE,"E86.MirrorC");var subQ1=sQuery(id+"F5.wireOp",EDGE,"E47.0.4");var subQ2=makeQuery(id+"F5.imprint","INTERSECT",VERTEX,{"disambiguationData":[OD(0.0)],"derivedFrom":[subQ1,subQ0]});Q36=makeQuery(id+"F5.imprint","IMPRINT",FACE,{"disambiguationData":[TD([[makeQuery(id+"F5.imprint","IMPRINT",EDGE,{"disambiguationData":[TD([[subQ2,-1.0]])],"derivedFrom":subQ1}),1.0]])]});}
            var Q37;
            {var subQ0=sQuery(id+"F5.wireOp",EDGE,"E86.MirrorC");var subQ1=sQuery(id+"F5.wireOp",EDGE,"E47.0.4");var subQ2=makeQuery(id+"F5.imprint","INTERSECT",VERTEX,{"disambiguationData":[OD(0.0)],"derivedFrom":[subQ1,subQ0]});Q37=makeQuery(id+"F5.imprint","IMPRINT",FACE,{"disambiguationData":[TD([[makeQuery(id+"F5.imprint","IMPRINT",EDGE,{"disambiguationData":[TD([[subQ2,-1.0]])],"derivedFrom":subQ1}),-1.0]])]});}
            var Q38;
            {var subQ0=sQuery(id+"F5.wireOp",EDGE,"E87.MirrorC");var subQ1=sQuery(id+"F5.wireOp",EDGE,"E47.0.4");var subQ2=makeQuery(id+"F5.imprint","INTERSECT",VERTEX,{"disambiguationData":[OD(0.0)],"derivedFrom":[subQ1,subQ0]});Q38=makeQuery(id+"F5.imprint","IMPRINT",FACE,{"disambiguationData":[TD([[makeQuery(id+"F5.imprint","IMPRINT",EDGE,{"disambiguationData":[TD([[subQ2,-1.0]])],"derivedFrom":subQ1}),1.0]])]});}
            var Q39;
            {var subQ0=sQuery(id+"F5.wireOp",EDGE,"E87.MirrorC");var subQ1=sQuery(id+"F5.wireOp",EDGE,"E47.0.4");var subQ2=makeQuery(id+"F5.imprint","INTERSECT",VERTEX,{"disambiguationData":[OD(0.0)],"derivedFrom":[subQ1,subQ0]});Q39=makeQuery(id+"F5.imprint","IMPRINT",FACE,{"disambiguationData":[TD([[makeQuery(id+"F5.imprint","IMPRINT",EDGE,{"disambiguationData":[TD([[subQ2,-1.0]])],"derivedFrom":subQ1}),-1.0]])]});}
            var Q40;
            {var subQ0=sQuery(id+"F5.wireOp",EDGE,"E88.MirrorC");var subQ1=sQuery(id+"F5.wireOp",EDGE,"E47.0.4");var subQ2=makeQuery(id+"F5.imprint","INTERSECT",VERTEX,{"disambiguationData":[OD(0.0)],"derivedFrom":[subQ1,subQ0]});Q40=makeQuery(id+"F5.imprint","IMPRINT",FACE,{"disambiguationData":[TD([[makeQuery(id+"F5.imprint","IMPRINT",EDGE,{"disambiguationData":[TD([[subQ2,-1.0]])],"derivedFrom":subQ1}),1.0]])]});}
            var Q41;
            {var subQ0=sQuery(id+"F5.wireOp",EDGE,"E88.MirrorC");var subQ1=sQuery(id+"F5.wireOp",EDGE,"E47.0.4");var subQ2=makeQuery(id+"F5.imprint","INTERSECT",VERTEX,{"disambiguationData":[OD(0.0)],"derivedFrom":[subQ1,subQ0]});Q41=makeQuery(id+"F5.imprint","IMPRINT",FACE,{"disambiguationData":[TD([[makeQuery(id+"F5.imprint","IMPRINT",EDGE,{"disambiguationData":[TD([[subQ2,-1.0]])],"derivedFrom":subQ1}),-1.0]])]});}
            var Q42;
            {var subQ0=sQuery(id+"F5.wireOp",EDGE,"E89.MirrorC");var subQ1=sQuery(id+"F5.wireOp",EDGE,"E47.0.4");var subQ2=makeQuery(id+"F5.imprint","INTERSECT",VERTEX,{"disambiguationData":[OD(0.0)],"derivedFrom":[subQ1,subQ0]});Q42=makeQuery(id+"F5.imprint","IMPRINT",FACE,{"disambiguationData":[TD([[makeQuery(id+"F5.imprint","IMPRINT",EDGE,{"disambiguationData":[TD([[subQ2,-1.0]])],"derivedFrom":subQ1}),1.0]])]});}
            var Q43;
            {var subQ0=sQuery(id+"F5.wireOp",EDGE,"E89.MirrorC");var subQ1=sQuery(id+"F5.wireOp",EDGE,"E47.0.4");var subQ2=makeQuery(id+"F5.imprint","INTERSECT",VERTEX,{"disambiguationData":[OD(0.0)],"derivedFrom":[subQ1,subQ0]});Q43=makeQuery(id+"F5.imprint","IMPRINT",FACE,{"disambiguationData":[TD([[makeQuery(id+"F5.imprint","IMPRINT",EDGE,{"disambiguationData":[TD([[subQ2,-1.0]])],"derivedFrom":subQ1}),-1.0]])]});}
            var Q44;
            {var subQ0=sQuery(id+"F5.wireOp",EDGE,"E90.MirrorC");var subQ1=sQuery(id+"F5.wireOp",EDGE,"E47.0.4");var subQ2=makeQuery(id+"F5.imprint","INTERSECT",VERTEX,{"disambiguationData":[OD(0.0)],"derivedFrom":[subQ1,subQ0]});Q44=makeQuery(id+"F5.imprint","IMPRINT",FACE,{"disambiguationData":[TD([[makeQuery(id+"F5.imprint","IMPRINT",EDGE,{"disambiguationData":[TD([[subQ2,-1.0]])],"derivedFrom":subQ1}),1.0]])]});}
            var Q45;
            {var subQ0=sQuery(id+"F5.wireOp",EDGE,"E90.MirrorC");var subQ1=sQuery(id+"F5.wireOp",EDGE,"E47.0.4");var subQ2=makeQuery(id+"F5.imprint","INTERSECT",VERTEX,{"disambiguationData":[OD(0.0)],"derivedFrom":[subQ1,subQ0]});Q45=makeQuery(id+"F5.imprint","IMPRINT",FACE,{"disambiguationData":[TD([[makeQuery(id+"F5.imprint","IMPRINT",EDGE,{"disambiguationData":[TD([[subQ2,-1.0]])],"derivedFrom":subQ1}),-1.0]])]});}
            var Q46;
            {var subQ0=sQuery(id+"F5.wireOp",EDGE,"E41.0");var subQ1=sQuery(id+"F5.wireOp",EDGE,"E28.0");var subQ2=makeQuery(id+"F5.imprint","INTERSECT",VERTEX,{"derivedFrom":[subQ1,subQ0,sQuery(id+"F5.wireOp",EDGE,"E47.0.0")]});Q46=makeQuery(id+"F5.imprint","IMPRINT",FACE,{"disambiguationData":[TD([[makeQuery(id+"F5.imprint","IMPRINT",EDGE,{"disambiguationData":[TD([[subQ2,1.0]])],"derivedFrom":subQ1}),-1.0]])]});}
            var Q47;
            {var subQ0=sQuery(id+"F5.wireOp",EDGE,"E41.0");var subQ1=sQuery(id+"F5.wireOp",EDGE,"E28.0");var subQ2=makeQuery(id+"F5.imprint","INTERSECT",VERTEX,{"derivedFrom":[subQ1,subQ0,sQuery(id+"F5.wireOp",EDGE,"E47.0.0")]});Q47=makeQuery(id+"F5.imprint","IMPRINT",FACE,{"disambiguationData":[TD([[makeQuery(id+"F5.imprint","IMPRINT",EDGE,{"disambiguationData":[TD([[subQ2,1.0]])],"derivedFrom":subQ1}),1.0]])]});}
            var Q48;
            {var subQ0=sQuery(id+"F5.wireOp",EDGE,"E28.0");var subQ1=sQuery(id+"F5.wireOp",EDGE,"E29.0");var subQ2=makeQuery(id+"F5.imprint","INTERSECT",VERTEX,{"derivedFrom":[subQ1,subQ0]});Q48=makeQuery(id+"F5.imprint","IMPRINT",FACE,{"disambiguationData":[TD([[makeQuery(id+"F5.imprint","IMPRINT",EDGE,{"disambiguationData":[TD([[subQ2,-1.0]])],"derivedFrom":subQ1}),-1.0]])]});}
            var Q49;
            {var subQ0=sQuery(id+"F5.wireOp",EDGE,"E28.0");var subQ1=sQuery(id+"F5.wireOp",EDGE,"E29.0");var subQ2=makeQuery(id+"F5.imprint","INTERSECT",VERTEX,{"derivedFrom":[subQ1,subQ0]});Q49=makeQuery(id+"F5.imprint","IMPRINT",FACE,{"disambiguationData":[TD([[makeQuery(id+"F5.imprint","IMPRINT",EDGE,{"disambiguationData":[TD([[subQ2,-1.0]])],"derivedFrom":subQ1}),1.0]])]});}
            var Q50;
            Q50=makeQuery(id+"F5.imprint","IMPRINT",FACE,{"disambiguationData":[TD([[makeQuery(id+"F5.imprint","IMPRINT",EDGE,{"derivedFrom":sQuery(id+"F5.wireOp",EDGE,"E43.0")}),-1.0]])]});
            var Q51;
            Q51=makeQuery(id+"F5.imprint","IMPRINT",FACE,{"disambiguationData":[TD([[makeQuery(id+"F5.imprint","IMPRINT",EDGE,{"derivedFrom":sQuery(id+"F5.wireOp",EDGE,"E46.0")}),1.0]])]});
            var Q52;
            Q52=makeQuery(id+"F5.imprint","IMPRINT",FACE,{"disambiguationData":[TD([[makeQuery(id+"F5.imprint","IMPRINT",EDGE,{"derivedFrom":sQuery(id+"F5.wireOp",EDGE,"E45.0")}),-1.0]])]});
            var Q53;
            {var subQ0=sQuery(id+"F5.wireOp",EDGE,"E42.0");var subQ1=sQuery(id+"F5.wireOp",EDGE,"E28.0");var subQ2=makeQuery(id+"F5.imprint","INTERSECT",VERTEX,{"derivedFrom":[subQ1,subQ0,sQuery(id+"F5.wireOp",EDGE,"E47.0.2")]});Q53=makeQuery(id+"F5.imprint","IMPRINT",FACE,{"disambiguationData":[TD([[makeQuery(id+"F5.imprint","IMPRINT",EDGE,{"disambiguationData":[TD([[subQ2,1.0]])],"derivedFrom":subQ1}),1.0]])]});}
            var Q54;
            {var subQ0=sQuery(id+"F5.wireOp",EDGE,"E42.0");var subQ1=sQuery(id+"F5.wireOp",EDGE,"E28.0");var subQ2=makeQuery(id+"F5.imprint","INTERSECT",VERTEX,{"derivedFrom":[subQ1,subQ0,sQuery(id+"F5.wireOp",EDGE,"E47.0.2")]});Q54=makeQuery(id+"F5.imprint","IMPRINT",FACE,{"disambiguationData":[TD([[makeQuery(id+"F5.imprint","IMPRINT",EDGE,{"disambiguationData":[TD([[subQ2,1.0]])],"derivedFrom":subQ1}),-1.0]])]});}
            var Q55;
            {var subQ0=sQuery(id+"F5.wireOp",EDGE,"E47.0.9");Q55=makeQuery(id+"F5.imprint","IMPRINT",FACE,{"disambiguationData":[TD([[makeQuery(id+"F5.imprint","IMPRINT",EDGE,{"derivedFrom":subQ0}),1.0]])]});}
            var Q56;
            {var subQ1=sQuery(id+"F5.wireOp",EDGE,"E44.0.2");Q56=makeQuery(id+"F5.imprint","IMPRINT",FACE,{"disambiguationData":[TD([[makeQuery(id+"F5.imprint","IMPRINT",EDGE,{"derivedFrom":subQ1}),1.0]])]});}
            var Q57;
            Q57=makeQuery(id+"F5.imprint","IMPRINT",FACE,{"disambiguationData":[TD([[makeQuery(id+"F5.imprint","IMPRINT",EDGE,{"derivedFrom":sQuery(id+"F5.wireOp",EDGE,"E38.0")}),1.0]])]});
            var Q58;
            Q58=makeQuery(id+"F5.imprint","IMPRINT",FACE,{"disambiguationData":[TD([[makeQuery(id+"F5.imprint","IMPRINT",EDGE,{"derivedFrom":sQuery(id+"F5.wireOp",EDGE,"E39.0")}),1.0]])]});
            var Q59;
            Q59=makeQuery(id+"F5.imprint","IMPRINT",FACE,{"disambiguationData":[TD([[makeQuery(id+"F5.imprint","IMPRINT",EDGE,{"derivedFrom":sQuery(id+"F5.wireOp",EDGE,"E40.0")}),-1.0]])]});
            var Q60;
            Q60=makeQuery(id+"F2.opShell","OFFSET_FACE",FACE,{"disambiguationData":[OSD([sQuery(id+"F0.wireOp",EDGE,"E0.top")])]});
            extrude(context, id + "F6", {"entities" : qUnion([Q0, Q1, Q2, Q3, Q4, Q5, Q6, Q7, Q8, Q9, Q10, Q11, Q12, Q13, Q14, Q15, Q16, Q17, Q18, Q19, Q20, Q21, Q22, Q23, Q24, Q25, Q26, Q27, Q28, Q29, Q30, Q31, Q32, Q33, Q34, Q35, Q36, Q37, Q38, Q39, Q40, Q41, Q42, Q43, Q44, Q45, Q46, Q47, Q48, Q49, Q50, Q51, Q52, Q53, Q54, Q55, Q56, Q57, Q58, Q59]), "operationType" : NewBodyOperationType.REMOVE, "endBound" : BoundingType.UP_TO_SURFACE, "oppositeDirection" : true, "endBoundEntityFace" : qUnion([Q60]), "depth" : 25.4 * mm});
        }
    });
